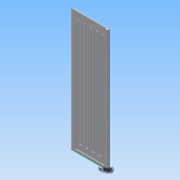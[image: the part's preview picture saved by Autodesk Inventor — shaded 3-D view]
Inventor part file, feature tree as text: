
AUTODESK INVENTOR PART (.ipt)
format: ipt  version: 2013 (Build 170138000, 138)  size: 223,744 bytes
history: native  units: in
note: dims shown in document units (in); Inventor stores cm internally (conversion verified against a paired STEP export)
features: other x7, extrude x3, sketch x3
ambient origin geometry x8: Origin, YZ Plane, XZ Plane, XY Plane, X Axis, Y Axis, Z Axis, Center Point
bodies: Solid1 (feature_tree)
feature tree (13):
  other  "Blocks"
  extrude  "Extrusion1"  Depth=78.0in
  extrude  "Extrusion3"  Depth=66.0in
  extrude  "Extrusion4"  Depth=2.9in
  sketch  "Sketch5"  dims[d6=1.0in d7=2.9in d9=0.24in d10=0.24in d18=1.5in d19=78.0in d20=78.0in d21=22.3125in d22=66.0in d23=2.0in d25=0.24in d26=0.24in d29=2.0in d31=1.5in d32=3.3in d33=1.74in d34=1.0in d35=0.1875in d37=5.46in d38=6.54in d41=66.0in d42=2.0in d43=0.24in d44=0.24in d45=2.0in d46=66.0in d47=2.0in d48=0.48in d49=66.0in d50=2.0in d51=1.0in d52=0.24in d53=0.24in d54=66.0in d55=0.48in d63=0.5in d64=0.0in d65=0.75in d67=1.5in d68=1.0in d69=0.0in d73=0.55in d74=0.47in d75=0.5in d76=0.58in d79=1.5in d80=0.48in d81=0.5in d82=0.25in d83=0.5118in d84=0.375in d85=0.2in d86=0.6056in d87=1.1056in]
  sketch  "Sketch1"  dims[d1=23.8125in d2=78.0in]
  other  "LEDPocket"
  other  "TwoLineColumn"
  other  "TwoLineColumnEnd"
  sketch  "Sketch4"  dims[d3=0.0in d4=66.0in]
  other  "15mm Neon profile"
  other  "15mm Neon profile:1"
  other  "15mm Neon profile:2"
